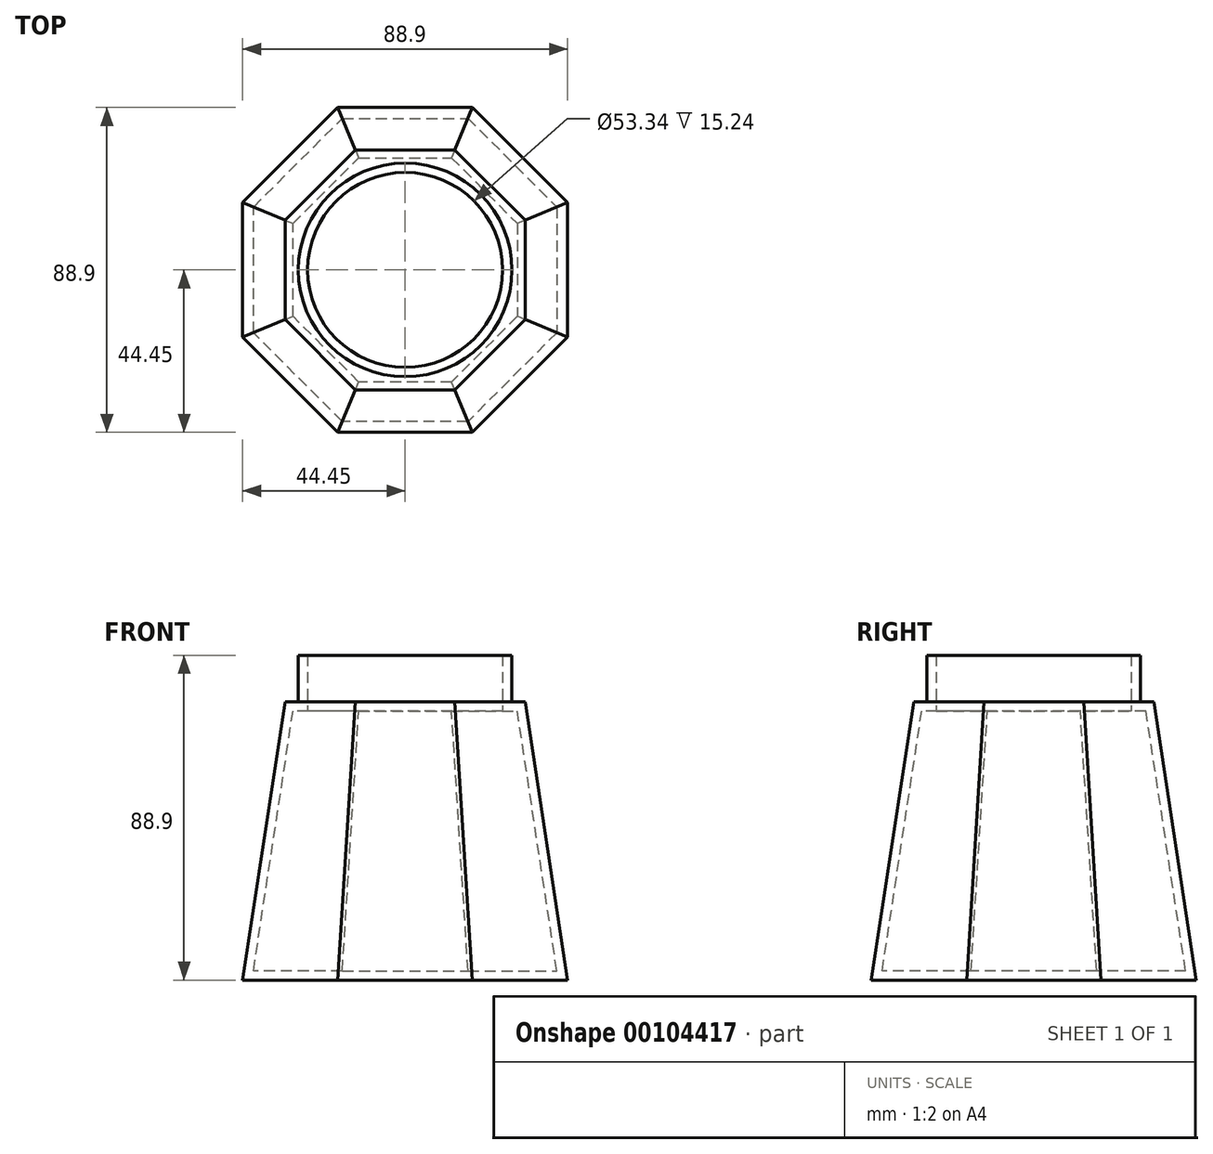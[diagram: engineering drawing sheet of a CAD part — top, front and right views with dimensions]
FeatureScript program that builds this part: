
annotation { "Feature Type Name" : "Feature", "Feature Type Description" : "" }
export const myFeature = defineFeature(function(context is Context, id is Id, definition is map)
    precondition{}
    {
        {
            var Q0;
            Q0=qCreatedBy(makeId("Top.planeOp"),FACE);
            var sketch = newSketch(context, id + "F0", { "sketchPlane" : qUnion([Q0])});
            skCircle(sketch, "E0.cCircle", {"center": v(0, 0) * mm, "radius": 44.45 * mm, "construction": true});
            skLineSegment(sketch, "E0.0", {"start": v(-18.41, 44.45) * mm, "end": v(18.41, 44.45) * mm});
            skLineSegment(sketch, "E0.1", {"start": v(18.41, 44.45) * mm, "end": v(44.45, 18.41) * mm});
            skLineSegment(sketch, "E0.2", {"start": v(44.45, 18.41) * mm, "end": v(44.45, -18.41) * mm});
            skLineSegment(sketch, "E0.3", {"start": v(44.45, -18.41) * mm, "end": v(18.41, -44.45) * mm});
            skLineSegment(sketch, "E0.4", {"start": v(18.41, -44.45) * mm, "end": v(-18.41, -44.45) * mm});
            skLineSegment(sketch, "E0.5", {"start": v(-18.41, -44.45) * mm, "end": v(-44.45, -18.41) * mm});
            skLineSegment(sketch, "E0.6", {"start": v(-44.45, -18.41) * mm, "end": v(-44.45, 18.41) * mm});
            skLineSegment(sketch, "E0.7", {"start": v(-44.45, 18.41) * mm, "end": v(-18.41, 44.45) * mm});
            skPoint(sketch, "E0.0.midPoint", {"position": v(0, 44.45) * mm});
            skSolve(sketch);
        }
        {
            var Q0;
            Q0=qCreatedBy(makeId("Top.planeOp"),FACE);
            cPlane(context, id + "F1", {"entities" : qUnion([Q0]), "cplaneType" : CPlaneType.OFFSET, "offset" : 76.2 * mm, "width" : 152.4 * mm, "height" : 152.4 * mm});
        }
        {
            var Q0;
            Q0=qCreatedBy(id+"F1.planeOp",FACE);
            var sketch = newSketch(context, id + "F2", { "sketchPlane" : qUnion([Q0])});
            skCircle(sketch, "E1.cCircle", {"center": v(0, 0) * mm, "radius": 35.56 * mm, "construction": true});
            skLineSegment(sketch, "E1.0", {"start": v(32.85, 13.6) * mm, "end": v(32.85, -13.6) * mm});
            skLineSegment(sketch, "E1.1", {"start": v(32.85, -13.6) * mm, "end": v(13.6, -32.85) * mm});
            skLineSegment(sketch, "E1.2", {"start": v(13.6, -32.85) * mm, "end": v(-13.6, -32.85) * mm});
            skLineSegment(sketch, "E1.3", {"start": v(-13.6, -32.85) * mm, "end": v(-32.85, -13.6) * mm});
            skLineSegment(sketch, "E1.4", {"start": v(-32.85, -13.6) * mm, "end": v(-32.85, 13.6) * mm});
            skLineSegment(sketch, "E1.5", {"start": v(-32.85, 13.6) * mm, "end": v(-13.6, 32.85) * mm});
            skLineSegment(sketch, "E1.6", {"start": v(-13.6, 32.85) * mm, "end": v(13.6, 32.85) * mm});
            skLineSegment(sketch, "E1.7", {"start": v(13.6, 32.85) * mm, "end": v(32.85, 13.6) * mm});
            skSolve(sketch);
        }
        {
            var Q0;
            Q0=makeQuery(id+"F0.imprint","IMPRINT",FACE,{"disambiguationData":[TD([[makeQuery(id+"F0.imprint","IMPRINT",EDGE,{"derivedFrom":sQuery(id+"F0.wireOp",EDGE,"E0.0")}),-1.0]])]});
            var Q1;
            Q1=makeQuery(id+"F2.imprint","IMPRINT",FACE,{"disambiguationData":[TD([[makeQuery(id+"F2.imprint","IMPRINT",EDGE,{"derivedFrom":sQuery(id+"F2.wireOp",EDGE,"E1.0")}),-1.0]])]});
            loft(context, id + "F3", {"sheetProfilesArray" : [{ "sheetProfileEntities" : qUnion([Q0]) }, { "sheetProfileEntities" : qUnion([Q1]) }]});
        }
        {
            var Q0;
            Q0=makeQuery(id+"F3.opLoft","CAP_FACE",FACE,{"disambiguationData":[OSD([makeQuery(id+"F2.imprint","IMPRINT",FACE,{"disambiguationData":[TD([[makeQuery(id+"F2.imprint","IMPRINT",EDGE,{"derivedFrom":sQuery(id+"F2.wireOp",EDGE,"E1.0")}),-1.0]])]})])],"isStart":true});
            var sketch = newSketch(context, id + "F4", { "sketchPlane" : qUnion([Q0])});
            skCircle(sketch, "E2", {"center": v(0, 0) * mm, "radius": 29.21 * mm});
            skSolve(sketch);
        }
        {
            var Q0;
            {var subQ0=sQuery(id+"F4.wireOp",EDGE,"E2");var subQ1=sQuery(id+"F2.wireOp",EDGE,"E1.6");var subQ7=sQuery(id+"F2.wireOp",EDGE,"E1.7");var subQ9=sQuery(id+"F2.wireOp",EDGE,"E1.0");var subQ10=makeQuery(id+"F4.imprint","INTERSECT",VERTEX,{"derivedFrom":[makeQuery(id+"F3.opLoft","MID_CAP_EDGE",EDGE,{"disambiguationData":[OSD([subQ9,subQ1,subQ7])],"capPos":1.0}),subQ0]});Q0=makeQuery(id+"F4.imprint","IMPRINT",FACE,{"disambiguationData":[TD([[makeQuery(id+"F4.imprint","IMPRINT",EDGE,{"disambiguationData":[TD([[subQ10,1.0]])],"derivedFrom":subQ0}),1.0]])]});}
            extrude(context, id + "F5", {"entities" : qUnion([Q0]), "operationType" : NewBodyOperationType.ADD, "depth" : 12.7 * mm});
        }
        {
            var Q0;
            Q0=makeQuery(id+"F5.opExtrude","CAP_FACE",FACE,{"disambiguationData":[OSD([sQuery(id+"F4.wireOp",EDGE,"E2")])],"isStart":false});
            shell(context, id + "F6", {"entities" : qUnion([Q0]), "thickness" : 2.54 * mm});
        }
    });
